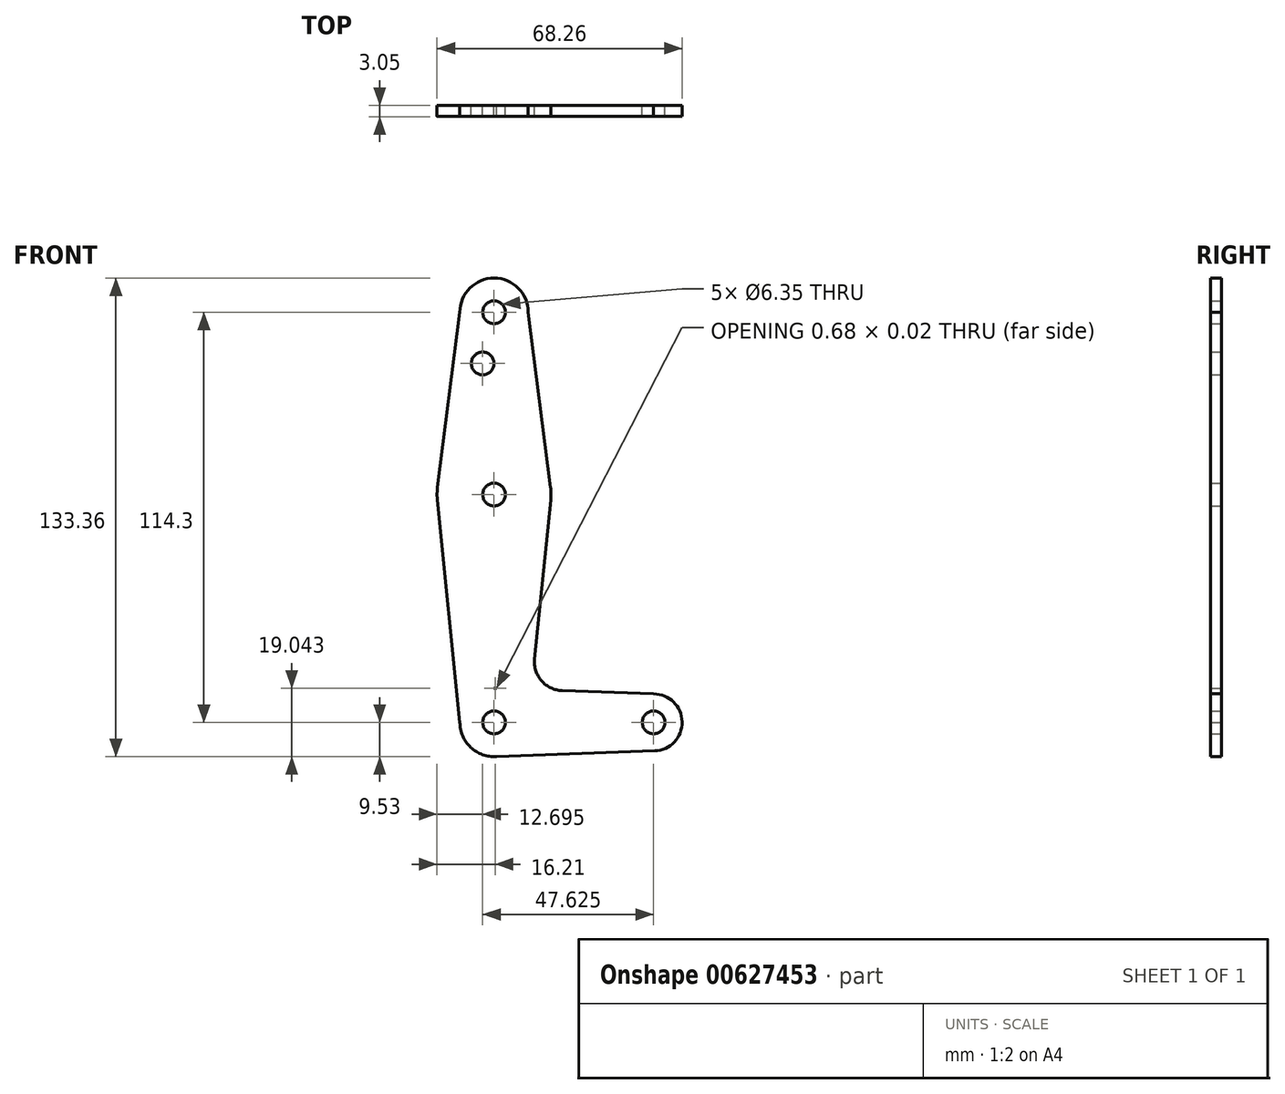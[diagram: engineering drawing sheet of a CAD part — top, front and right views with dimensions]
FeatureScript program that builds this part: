
annotation { "Feature Type Name" : "Feature", "Feature Type Description" : "" }
export const myFeature = defineFeature(function(context is Context, id is Id, definition is map)
    precondition{}
    {
        {
            var Q0;
            Q0=qCreatedBy(makeId("Front.planeOp"),FACE);
            var sketch = newSketch(context, id + "F0", { "sketchPlane" : qUnion([Q0])});
            skPoint(sketch, "E0.endSnap0", {"position": v(0, 0) * mm});
            skLineSegment(sketch, "E1", {"start": v(0, 0) * mm, "end": v(0, 114.3) * mm, "construction": true});
            skLineSegment(sketch, "E2", {"start": v(0, 0) * mm, "end": v(44.45, 0) * mm, "construction": true});
            skCircle(sketch, "E3", {"center": v(0, 114.3) * mm, "radius": 9.53 * mm});
            skCircle(sketch, "E4", {"center": v(0, 63.5) * mm, "radius": 15.88 * mm});
            skCircle(sketch, "E5", {"center": v(0, 0) * mm, "radius": 9.53 * mm});
            skCircle(sketch, "E6", {"center": v(44.45, 0) * mm, "radius": 7.94 * mm});
            skCircle(sketch, "E7", {"center": v(0, 114.3) * mm, "radius": 3.18 * mm});
            skCircle(sketch, "E8", {"center": v(0, 63.5) * mm, "radius": 3.18 * mm});
            skCircle(sketch, "E9", {"center": v(0, 0) * mm, "radius": 3.18 * mm});
            skCircle(sketch, "E10", {"center": v(44.45, 0) * mm, "radius": 3.18 * mm});
            skCircle(sketch, "E11", {"center": v(-3.18, 100.03) * mm, "radius": 3.18 * mm});
            skLineSegment(sketch, "E12", {"start": v(-9.52, 114.3) * mm, "end": v(-15.75, 65.5) * mm});
            skLineSegment(sketch, "E13", {"start": v(9.53, 114.3) * mm, "end": v(15.75, 65.5) * mm});
            skLineSegment(sketch, "E14", {"start": v(-9.52, 0) * mm, "end": v(-15.8, 61.9) * mm});
            skLineSegment(sketch, "E15", {"start": v(15.8, 61.9) * mm, "end": v(11.3, 17.6) * mm});
            skLineSegment(sketch, "E16", {"start": v(0, -9.53) * mm, "end": v(44.73, -7.93) * mm});
            skLineSegment(sketch, "E17", {"start": v(44.45, 7.94) * mm, "end": v(18.93, 8.85) * mm});
            skLineSegment(sketch, "E18.trimOffspring", {"start": v(0.68, 9.5) * mm, "end": v(0, 9.52) * mm});
            skPoint(sketch, "E19.visualSharp", {"position": v(10.45, 9.15) * mm});
            skArc(sketch, "E19.filletArc", {"start": v(11.3, 17.6) * mm, "mid": v(13.22, 11.57) * mm, "end": v(18.93, 8.85) * mm});
            skSolve(sketch);
        }
        {
            var Q0;
            Q0 = qSketchRegion(id + "F0", true);
            extrude(context, id + "F1", {"entities" : qUnion([Q0]), "depth" : 3.05 * mm, "offsetDistance" : 25.4 * mm});
        }
    });
